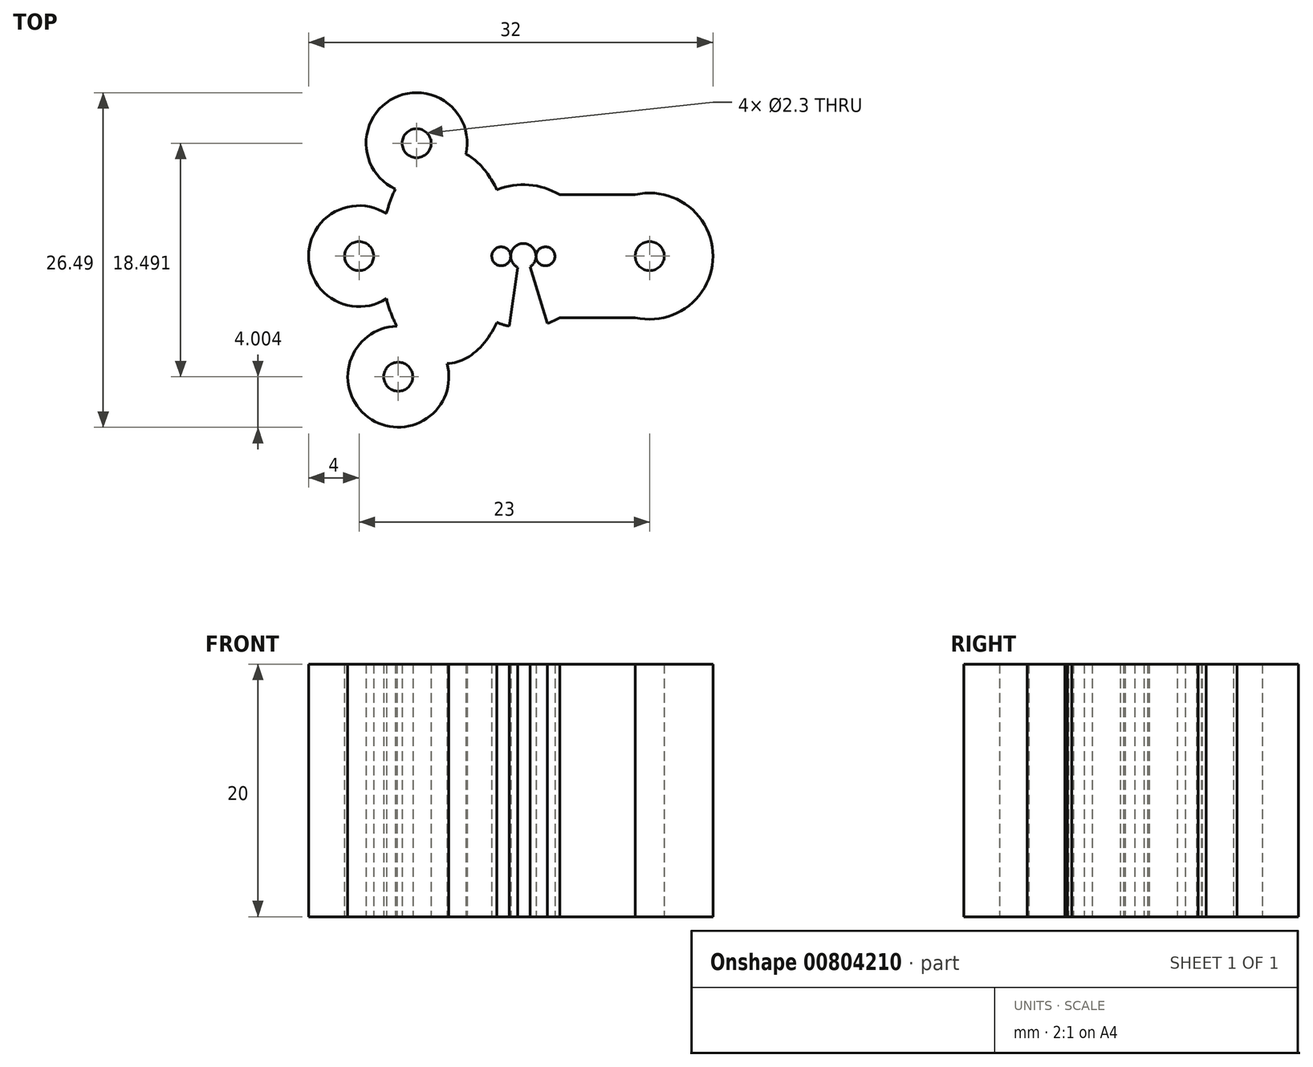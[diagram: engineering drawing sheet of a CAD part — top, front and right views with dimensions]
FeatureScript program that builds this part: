
annotation { "Feature Type Name" : "Feature", "Feature Type Description" : "" }
export const myFeature = defineFeature(function(context is Context, id is Id, definition is map)
    precondition{}
    {
        {
            var Q0;
            Q0=qCreatedBy(makeId("Top.planeOp"),FACE);
            var sketch = newSketch(context, id + "F0", { "sketchPlane" : qUnion([Q0])});
            skArc(sketch, "E0", {"start": v(0.54, -0.84) * mm, "mid": v(-0.06, 1) * mm, "end": v(-0.44, -0.9) * mm});
            skCircle(sketch, "E1", {"center": v(1.75, -0.01) * mm, "radius": 0.75 * mm});
            skPoint(sketch, "E1.first.point", {"position": v(1, 0) * mm});
            skPoint(sketch, "E1.second.point", {"position": v(2.12, -0.67) * mm});
            skPoint(sketch, "E1.third.point", {"position": v(2.31, 0.48) * mm});
            skCircle(sketch, "E2", {"center": v(-1.75, -0.02) * mm, "radius": 0.75 * mm});
            skPoint(sketch, "E2.first.point", {"position": v(-1, 0) * mm});
            skPoint(sketch, "E2.second.point", {"position": v(-1.8, -0.76) * mm});
            skPoint(sketch, "E2.third.point", {"position": v(-1.95, 0.7) * mm});
            skLineSegment(sketch, "E3", {"start": v(0, 0) * mm, "end": v(-13, 0) * mm, "construction": true});
            skCircle(sketch, "E4", {"center": v(-13, 0) * mm, "radius": 1.15 * mm});
            skLineSegment(sketch, "E5", {"start": v(0, 0) * mm, "end": v(10, 0) * mm, "construction": true});
            skCircle(sketch, "E6", {"center": v(10, 0) * mm, "radius": 1.15 * mm});
            skPoint(sketch, "E7.1.0", {"position": v(-0.7, -0.35) * mm});
            skCircle(sketch, "E7.1.1", {"center": v(-9.9, -9.55) * mm, "radius": 1.15 * mm});
            skPoint(sketch, "E7.2.0", {"position": v(-0.95, -1.1) * mm});
            skPoint(sketch, "E7.3.0", {"position": v(-0.6, -1.8) * mm});
            skPoint(sketch, "E7.4.0", {"position": v(0.15, -2.05) * mm});
            skPoint(sketch, "E7.5.0", {"position": v(0.85, -1.7) * mm});
            skPoint(sketch, "E7.6.0", {"position": v(1.1, -0.95) * mm});
            skPoint(sketch, "E7.7.0", {"position": v(0.75, -0.25) * mm});
            skCircle(sketch, "E7.7.1", {"center": v(-8.44, 8.94) * mm, "radius": 1.15 * mm});
            skPoint(sketch, "E7.center", {"position": v(0.07, -1.03) * mm});
            skArc(sketch, "E8", {"start": v(-4.54, 8.09) * mm, "mid": v(-10.22, 12.53) * mm, "end": v(-10.13, 5.32) * mm});
            skArc(sketch, "E9", {"start": v(-10.84, 3.37) * mm, "mid": v(-17, 0) * mm, "end": v(-10.84, -3.37) * mm});
            skArc(sketch, "E10", {"start": v(-10.02, -5.55) * mm, "mid": v(-12.28, -12.76) * mm, "end": v(-6.03, -8.5) * mm});
            skArc(sketch, "E11", {"start": v(2.87, 4.87) * mm, "mid": v(0.43, 5.64) * mm, "end": v(-2.1, 5.25) * mm});
            skArc(sketch, "E12", {"start": v(8.87, -4.87) * mm, "mid": v(15, 0) * mm, "end": v(8.87, 4.87) * mm});
            skPoint(sketch, "E13.middle", {"position": v(-7.05, 0) * mm});
            skLineSegment(sketch, "E14.bottom", {"start": v(8.87, -4.87) * mm, "end": v(2.87, -4.87) * mm});
            skLineSegment(sketch, "E14.top", {"start": v(8.87, 4.87) * mm, "end": v(2.87, 4.87) * mm});
            skPoint(sketch, "E14.middle", {"position": v(5.56, 0) * mm});
            skPoint(sketch, "E15.orphan", {"position": v(2.26, 4.87) * mm});
            skPoint(sketch, "E16.orphan", {"position": v(2.26, -4.87) * mm});
            skPoint(sketch, "E13.bottom.start.orphan", {"position": v(-4.38, -1.74) * mm});
            skPoint(sketch, "E13.top.start.orphan", {"position": v(-4.38, 1.74) * mm});
            skPoint(sketch, "E17.orphan", {"position": v(-9.72, 1.74) * mm});
            skPoint(sketch, "E18.trimOffspring.end.orphan", {"position": v(-9.72, -1.74) * mm});
            skEllipticalArc(sketch, "E19", {});
            skEllipticalArc(sketch, "E20.trimOffspring", {});
            skArc(sketch, "E21.trimOffspring", {"start": v(-2.1, -5.25) * mm, "mid": v(-1.62, -5.42) * mm, "end": v(-1.12, -5.54) * mm});
            skEllipticalArc(sketch, "E22.trimOffspring", {});
            skEllipticalArc(sketch, "E23.trimOffspring", {});
            skEllipticalArc(sketch, "E24.trimOffspring", {});
            skLineSegment(sketch, "E25", {"start": v(0.54, -0.84) * mm, "end": v(1.9, -5.33) * mm});
            skLineSegment(sketch, "E26", {"start": v(-0.44, -0.9) * mm, "end": v(-1.12, -5.54) * mm});
            skArc(sketch, "E27.trimOffspring", {"start": v(1.9, -5.33) * mm, "mid": v(2.4, -5.12) * mm, "end": v(2.87, -4.87) * mm});
            const initialGuessF0  = {"E19": [-0.006128806831687689, 0, 0, -1, 0.00850704126060009, 0.005128806831687689, 4.037082700511179, 4.30558298285382], "E20.trimOffspring": [-0.006128806831687689, 0, 0, -1, 0.00850704126060009, 0.005128806831687689, 5.119194977915559, 5.422791387259391], "E22.trimOffspring": [-0.006128806831687689, 0, 0, -1, 0.00850704126060009, 0.005128806831687689, 2.2360603492002515, 2.826197360965257], "E23.trimOffspring": [-0.006128806831687689, 0, 0, -1, 0.00850704126060009, 0.005128806831687689, 1.5668520021530838, 1.5707963267948966], "E24.trimOffspring": [-0.006128806831687689, 0, 0, -1, 0.00850704126060009, 0.005128806831687689, 0.018563120917778137, 0.9055323043895418]};
            skSetInitialGuess(sketch, initialGuessF0);
            skSolve(sketch);
        }
        {
            var Q0;
            Q0=makeQuery(id+"F0.imprint","IMPRINT",FACE,{"disambiguationData":[TD([[makeQuery(id+"F0.imprint","IMPRINT",EDGE,{"derivedFrom":sQuery(id+"F0.wireOp",EDGE,"E4")}),-1.0]])]});
            extrude(context, id + "F1", {"entities" : qUnion([Q0]), "depth" : 20 * mm, "offsetDistance" : 25 * mm});
        }
    });
